# Revit family: Faucet-Bath_Filler-KOHLER-COMPOSED-K-31138T
name_source: partatom
category: Plumbing Fixtures
revit_build: Autodesk Revit 2017 (Build: 20160225_1515(x64)
units: mm (PartAtom-declared; Revit-internal decimal feet)

## family parameters
Cut with Voids When Loaded = No
Host = Face
OmniClass Number = 23.31.11.00
OmniClass Title = Faucets
Part Type = Normal
Room Calculation Point = No
Round Connector Dimension = Use Diameter
Shared = No

## types (10) — shared parameters
ADA Compliant = No
Assembly Code = D2010
CW Connection = Yes
Cold Water Inlet = Cold Water Inlet
Date Modified = 09/29/2021
Default Elevation = 36"
Description = COMPOSED FREE STANDING WITHOUT HANDSHOWER
Drain Included = No
Flow Rate = 13 GPM
HW Connection = Yes
Handle Clearance = 2"
Height = 35 7/8"
Hot Water Inlet = Hot Water Inlet
Length = 8 1/4"
Manufacturer = KOHLER Co.
MasterFormat 1995 = 15410
MasterFormat 2004 = 22.41.39
Material = Premium Metal Construction
Pressure = 45.00 psi
Product Name = COMPOSED
Spout Reach = 8 1/4"
URL = http://www.kohler.com.cn
Vent Connection = No
Waste Connection = No
Waste Water Outlet = Waste Water Outlet
Width = 6 1/8"

## per-type parameters (varying)
| type | Finish | Model | Type |
| CP-Polished Chrome | Kohler-Metal-CP-Polished_Chrome | K-31138T-4-CP | 1 |
| BN-Roman Silver | Kohler-Metal-BN-Roman_Silver | K-31138T-4-BN | 2 |
| BL-Matte Black | Kohler-Metal-BL-Matte_Black | K-31138T-4-BL | 3 |
| BV-Roman Copper | Kohler-Metal-BV-Roman_Copper | K-31138T-4-BV | 4 |
| AF-Flange Gold | Kohler-Metal-AF-Flange_Gold | K-31138T-4-AF | 5 |
| SN-Champagne Gold | Kohler-Metal-SN-Champagne_Gold | K-31138T-4-SN | 6 |
| TT-Titanium Silver | Kohler-Metal-TT-Titanium_Silver | K-31138T-4-TT | 7 |
| 2MB-Vibrant Brushed Moderne Brass | Kohler-Metal-2MB-Vibrant_Brushed_Moderne_Brass | K-31138T-4-2MB | 8 |
| PGD-Eternal Gold | Kohler-Metal-PGD-Eternal_Gold | K-31138T-4-PGD | 9 |
| RGD-Rose Gold | Kohler-Metal-RGD-Rose_Gold | K-31138T-4-RGD | 10 |

## geometry (parser evidence)
native form markers: Sweep x3
no freeform markers — native parametric forms only
